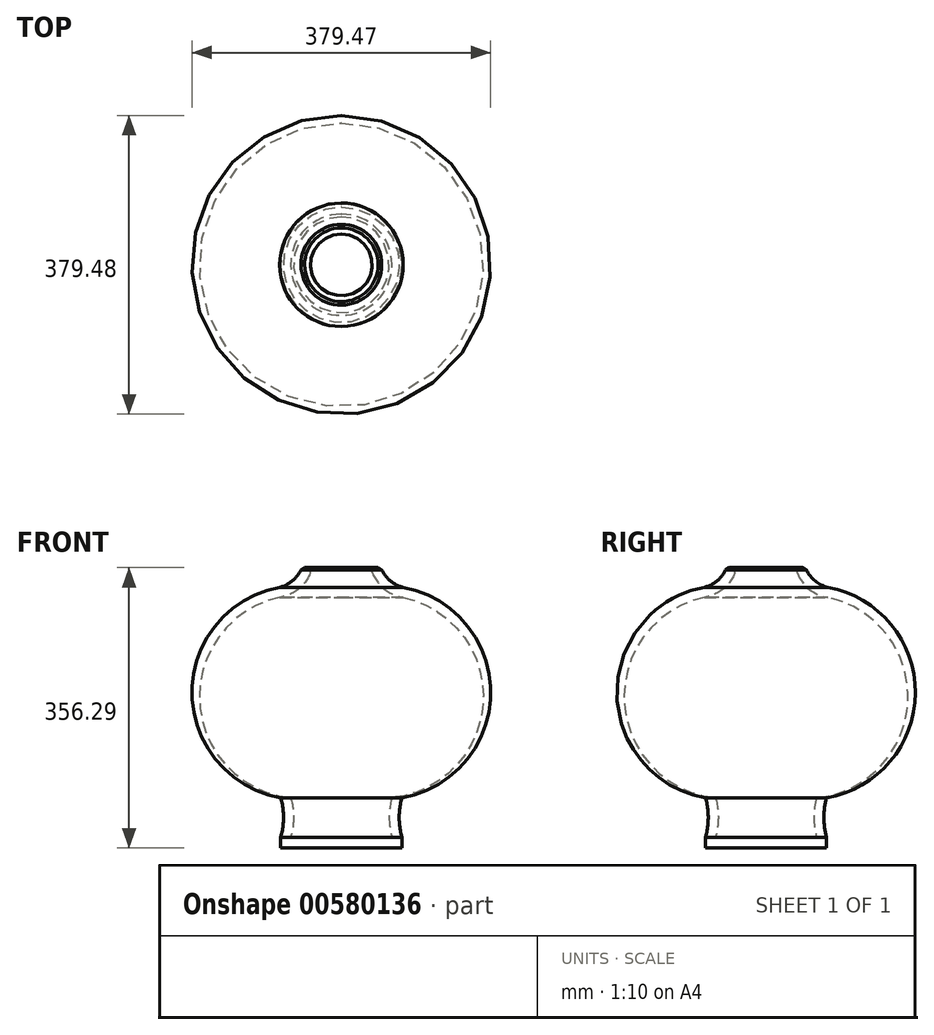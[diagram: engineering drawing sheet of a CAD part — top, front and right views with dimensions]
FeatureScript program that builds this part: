
annotation { "Feature Type Name" : "Feature", "Feature Type Description" : "" }
export const myFeature = defineFeature(function(context is Context, id is Id, definition is map)
    precondition{}
    {
        {
            var Q0;
            Q0=qCreatedBy(makeId("Right.planeOp"),FACE);
            var sketch = newSketch(context, id + "F0", { "sketchPlane" : qUnion([Q0])});
            skLineSegment(sketch, "E0", {"start": v(0, 0) * mm, "end": v(0, 54.4) * mm});
            skLineSegment(sketch, "E1", {"start": v(0, 54.4) * mm, "end": v(0, 0) * mm});
            skLineSegment(sketch, "E2", {"start": v(64.29, 0) * mm, "end": v(0, 0) * mm});
            skArc(sketch, "E3", {"start": v(64.29, 50.1) * mm, "mid": v(60.76, 25.05) * mm, "end": v(64.29, 0) * mm});
            skArc(sketch, "E4", {"start": v(64.29, 50.1) * mm, "mid": v(180.08, 171.28) * mm, "end": v(78.47, 304.58) * mm});
            skArc(sketch, "E5", {"start": v(37.33, 342.39) * mm, "mid": v(52.2, 317.28) * mm, "end": v(78.47, 304.58) * mm});
            skArc(sketch, "E6", {"start": v(50.03, 342.39) * mm, "mid": v(61.22, 326.4) * mm, "end": v(78.47, 317.28) * mm});
            skPoint(sketch, "E6.endSnap0", {"position": v(52.2, 317.28) * mm});
            skArc(sketch, "E7", {"start": v(76.99, 50.1) * mm, "mid": v(189.74, 183.07) * mm, "end": v(78.47, 317.28) * mm});
            skArc(sketch, "E8", {"start": v(76.99, 50.1) * mm, "mid": v(73.46, 25.05) * mm, "end": v(76.99, 0) * mm});
            skLineSegment(sketch, "E9", {"start": v(76.99, 0) * mm, "end": v(76.99, -13.9) * mm});
            skLineSegment(sketch, "E10", {"start": v(76.99, -13.9) * mm, "end": v(0, -13.9) * mm});
            skLineSegment(sketch, "E11", {"start": v(0, -13.9) * mm, "end": v(0, 0) * mm});
            skLineSegment(sketch, "E12", {"start": v(37.33, 342.39) * mm, "end": v(50.03, 342.39) * mm});
            skSolve(sketch);
        }
        {
            var Q0;
            Q0=makeQuery(id+"F0.imprint","IMPRINT",FACE,{"disambiguationData":[TD([[makeQuery(id+"F0.imprint","IMPRINT",EDGE,{"derivedFrom":sQuery(id+"F0.wireOp",EDGE,"E2")}),1.0]])]});
            extrude(context, id + "F1", {"entities" : qUnion([Q0]), "depth" : 0.25 * mm, "offsetDistance" : 25.4 * mm});
        }
        {
            var Q0;
            Q0=makeQuery(id+"F1.opExtrude","CAP_FACE",FACE,{"disambiguationData":[OSD([sQuery(id+"F0.wireOp",EDGE,"E2"),sQuery(id+"F0.wireOp",EDGE,"E3"),sQuery(id+"F0.wireOp",EDGE,"E4"),sQuery(id+"F0.wireOp",EDGE,"E5"),sQuery(id+"F0.wireOp",EDGE,"E6"),sQuery(id+"F0.wireOp",EDGE,"E7"),sQuery(id+"F0.wireOp",EDGE,"E8"),sQuery(id+"F0.wireOp",EDGE,"E9"),sQuery(id+"F0.wireOp",EDGE,"E10"),sQuery(id+"F0.wireOp",EDGE,"E11"),sQuery(id+"F0.wireOp",EDGE,"E12")])],"isStart":false});
            var Q1;
            Q1=makeQuery(id+"F1.opExtrude","CAP_EDGE",EDGE,{"disambiguationData":[OSD([sQuery(id+"F0.wireOp",EDGE,"E11")])],"isStart":false});
            revolve(context, id + "F2", {"operationType" : NewBodyOperationType.ADD, "entities" : qUnion([Q0]), "axis" : qUnion([Q1]), "revolveType" : RevolveType.FULL});
        }
        {
            var Q0;
            Q0=makeQuery(id+"F2.opRevolve","SWEPT_EDGE",EDGE,{"disambiguationData":[OSD([sQuery(id+"F0.wireOp",EDGE,"E5"),sQuery(id+"F0.wireOp",EDGE,"E12")])]});
            fillet(context, id + "F3", {"entities" : qUnion([Q0]), "radius" : 5.08 * mm, "tangentPropagation" : true, "allowEdgeOverflow" : false});
        }
        {
            var Q0;
            {var subQ0=sQuery(id+"F0.wireOp",EDGE,"E12");Q0=makeQuery(id+"F2.boolean.opBoolean","MERGE",FACE,{"derivedFrom":[makeQuery(id+"F1.opExtrude","SWEPT_FACE",FACE,{"disambiguationData":[OSD([subQ0])]}),makeQuery(id+"F2.opRevolve","SWEPT_FACE",FACE,{"disambiguationData":[OSD([subQ0])]})]});}
            chamfer(context, id + "F4", {"entities" : qUnion([Q0]), "width" : 5.08 * mm, "tangentPropagation" : true});
        }
    });
